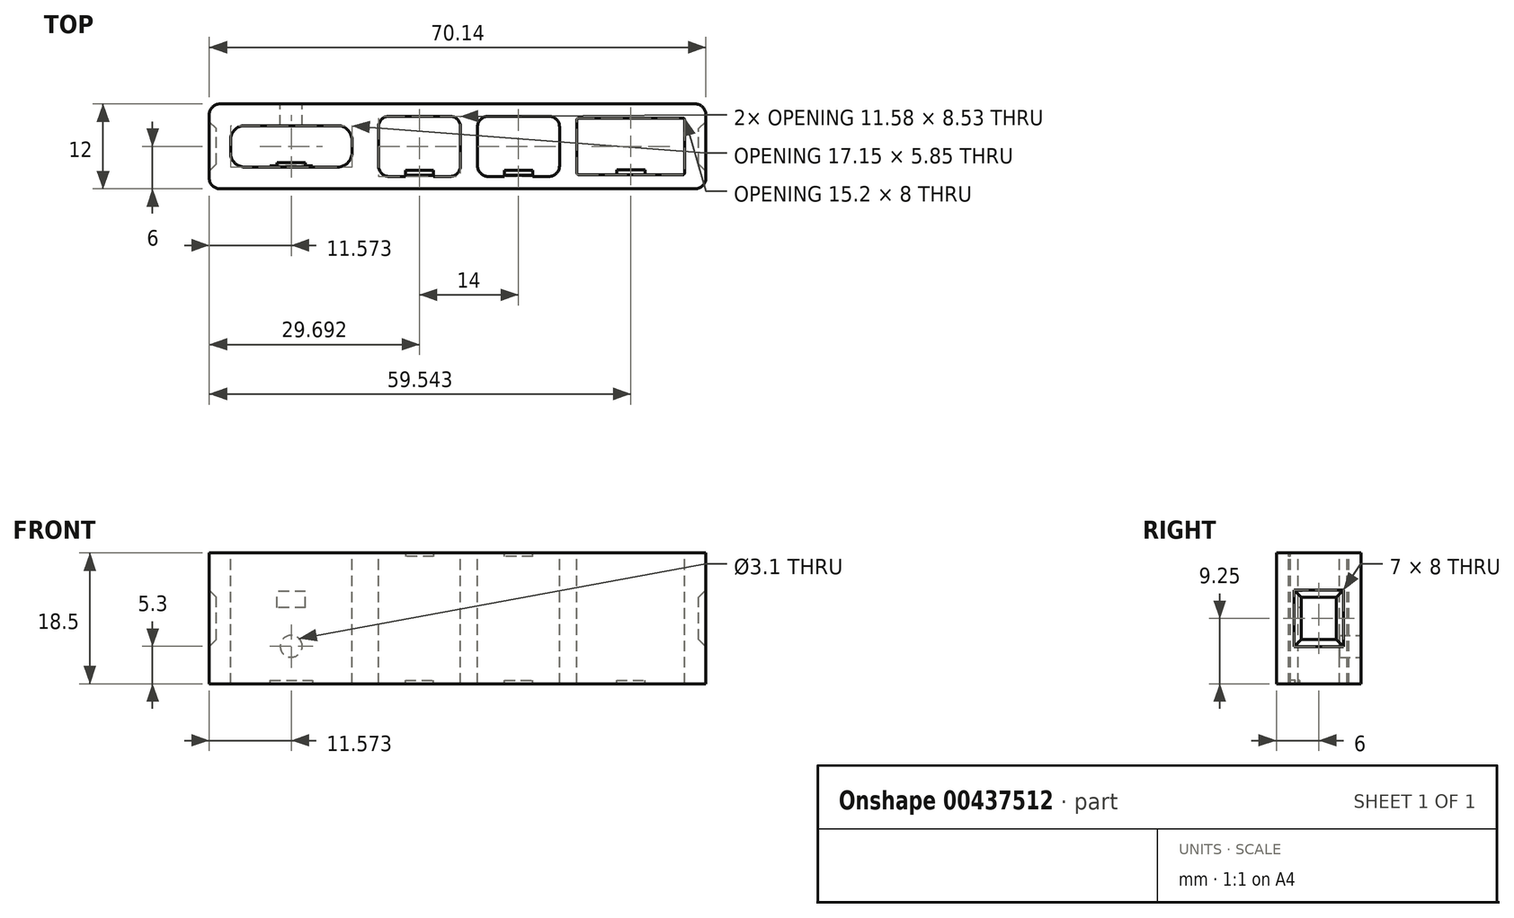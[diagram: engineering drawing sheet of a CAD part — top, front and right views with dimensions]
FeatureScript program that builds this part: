
annotation { "Feature Type Name" : "Feature", "Feature Type Description" : "" }
export const myFeature = defineFeature(function(context is Context, id is Id, definition is map)
    precondition{}
    {
        {
            assignVariable(context, id + "F0", {"name" : "TB1CableStopHeight", "anyValue" : .2});
        }
        {
            var Q0;
            Q0=qCreatedBy(makeId("Front.planeOp"),FACE);
            var sketch = newSketch(context, id + "F1", { "sketchPlane" : qUnion([Q0])});
            skLineSegment(sketch, "E0.bottom", {"start": v(33.57, -6) * mm, "end": v(-33.57, -6) * mm});
            skLineSegment(sketch, "E0.top", {"start": v(33.57, 6) * mm, "end": v(-33.57, 6) * mm});
            skLineSegment(sketch, "E0.left", {"start": v(35.07, -4.5) * mm, "end": v(35.07, 4.5) * mm});
            skLineSegment(sketch, "E0.right", {"start": v(-35.07, -4.5) * mm, "end": v(-35.07, 4.5) * mm});
            skPoint(sketch, "E0.middle", {"position": v(0, 0) * mm});
            skLineSegment(sketch, "E1", {"start": v(-35.07, 0) * mm, "end": v(35.07, 0) * mm, "construction": true});
            skLineSegment(sketch, "E2.bottom", {"start": v(-16.92, -2.92) * mm, "end": v(-30.07, -2.92) * mm});
            skLineSegment(sketch, "E2.top", {"start": v(-16.92, 2.93) * mm, "end": v(-30.07, 2.93) * mm});
            skLineSegment(sketch, "E2.left", {"start": v(-14.92, -0.92) * mm, "end": v(-14.92, 0.93) * mm});
            skLineSegment(sketch, "E2.right", {"start": v(-32.07, -0.92) * mm, "end": v(-32.07, 0.93) * mm});
            skPoint(sketch, "E2.middle", {"position": v(-23.5, 0) * mm});
            skLineSegment(sketch, "E3.bottom", {"start": v(-1.09, 4.26) * mm, "end": v(-9.67, 4.27) * mm});
            skLineSegment(sketch, "E3.top", {"start": v(-1.09, -4.26) * mm, "end": v(-9.67, -4.26) * mm});
            skLineSegment(sketch, "E3.left", {"start": v(0.41, 2.76) * mm, "end": v(0.41, -2.77) * mm});
            skLineSegment(sketch, "E3.right", {"start": v(-11.17, 2.76) * mm, "end": v(-11.17, -2.76) * mm});
            skPoint(sketch, "E3.middle", {"position": v(-5.38, 0) * mm});
            skLineSegment(sketch, "E4.bottom", {"start": v(12.91, 4.27) * mm, "end": v(4.33, 4.27) * mm});
            skLineSegment(sketch, "E4.top", {"start": v(12.91, -4.26) * mm, "end": v(4.33, -4.26) * mm});
            skLineSegment(sketch, "E4.left", {"start": v(14.41, 2.77) * mm, "end": v(14.41, -2.76) * mm});
            skLineSegment(sketch, "E4.right", {"start": v(2.83, 2.77) * mm, "end": v(2.83, -2.76) * mm});
            skPoint(sketch, "E4.middle", {"position": v(8.62, 0) * mm});
            skLineSegment(sketch, "E5.bottom", {"start": v(31.87, -4) * mm, "end": v(17.07, -4) * mm});
            skLineSegment(sketch, "E5.top", {"start": v(31.87, 4) * mm, "end": v(17.07, 4) * mm});
            skLineSegment(sketch, "E5.left", {"start": v(32.07, -3.8) * mm, "end": v(32.07, 3.8) * mm});
            skLineSegment(sketch, "E5.right", {"start": v(16.87, -3.8) * mm, "end": v(16.87, 3.8) * mm});
            skPoint(sketch, "E5.middle", {"position": v(24.47, 0) * mm});
            skPoint(sketch, "E6.visualSharp", {"position": v(-32.07, 2.93) * mm});
            skArc(sketch, "E6.filletArc", {"start": v(-30.07, 2.93) * mm, "mid": v(-31.49, 2.34) * mm, "end": v(-32.07, 0.93) * mm});
            skPoint(sketch, "E7.visualSharp", {"position": v(-14.92, 2.93) * mm});
            skArc(sketch, "E7.filletArc", {"start": v(-14.92, 0.93) * mm, "mid": v(-15.5, 2.34) * mm, "end": v(-16.92, 2.93) * mm});
            skPoint(sketch, "E8.visualSharp", {"position": v(-14.92, -2.92) * mm});
            skArc(sketch, "E8.filletArc", {"start": v(-16.92, -2.92) * mm, "mid": v(-15.5, -2.34) * mm, "end": v(-14.92, -0.92) * mm});
            skPoint(sketch, "E9.visualSharp", {"position": v(-32.07, -2.93) * mm});
            skArc(sketch, "E9.filletArc", {"start": v(-32.07, -0.92) * mm, "mid": v(-31.49, -2.34) * mm, "end": v(-30.07, -2.92) * mm});
            skPoint(sketch, "E10.visualSharp", {"position": v(-11.17, 4.27) * mm});
            skArc(sketch, "E10.filletArc", {"start": v(-9.67, 4.26) * mm, "mid": v(-10.73, 3.83) * mm, "end": v(-11.17, 2.77) * mm});
            skPoint(sketch, "E11.visualSharp", {"position": v(0.41, 4.26) * mm});
            skArc(sketch, "E11.filletArc", {"start": v(0.41, 2.76) * mm, "mid": v(-0.03, 3.83) * mm, "end": v(-1.09, 4.26) * mm});
            skPoint(sketch, "E12.visualSharp", {"position": v(-11.17, -4.26) * mm});
            skArc(sketch, "E12.filletArc", {"start": v(-11.17, -2.76) * mm, "mid": v(-10.73, -3.83) * mm, "end": v(-9.67, -4.26) * mm});
            skPoint(sketch, "E13.visualSharp", {"position": v(0.41, -4.27) * mm});
            skArc(sketch, "E13.filletArc", {"start": v(-1.09, -4.26) * mm, "mid": v(-0.03, -3.83) * mm, "end": v(0.41, -2.77) * mm});
            skPoint(sketch, "E14.visualSharp", {"position": v(2.83, 4.26) * mm});
            skArc(sketch, "E14.filletArc", {"start": v(4.33, 4.26) * mm, "mid": v(3.27, 3.83) * mm, "end": v(2.83, 2.77) * mm});
            skPoint(sketch, "E15.visualSharp", {"position": v(14.41, 4.27) * mm});
            skArc(sketch, "E15.filletArc", {"start": v(14.41, 2.77) * mm, "mid": v(13.97, 3.83) * mm, "end": v(12.91, 4.27) * mm});
            skPoint(sketch, "E16.visualSharp", {"position": v(14.41, -4.26) * mm});
            skArc(sketch, "E16.filletArc", {"start": v(12.91, -4.26) * mm, "mid": v(13.97, -3.83) * mm, "end": v(14.41, -2.76) * mm});
            skPoint(sketch, "E17.visualSharp", {"position": v(2.83, -4.26) * mm});
            skArc(sketch, "E17.filletArc", {"start": v(2.83, -2.76) * mm, "mid": v(3.27, -3.83) * mm, "end": v(4.33, -4.26) * mm});
            skPoint(sketch, "E18.visualSharp", {"position": v(16.87, 4) * mm});
            skArc(sketch, "E18.filletArc", {"start": v(17.07, 4) * mm, "mid": v(16.93, 3.94) * mm, "end": v(16.87, 3.8) * mm});
            skPoint(sketch, "E19.visualSharp", {"position": v(32.07, 4) * mm});
            skArc(sketch, "E19.filletArc", {"start": v(32.07, 3.8) * mm, "mid": v(32.01, 3.94) * mm, "end": v(31.87, 4) * mm});
            skPoint(sketch, "E20.visualSharp", {"position": v(32.07, -4) * mm});
            skArc(sketch, "E20.filletArc", {"start": v(31.87, -4) * mm, "mid": v(32.01, -3.94) * mm, "end": v(32.07, -3.8) * mm});
            skPoint(sketch, "E21.visualSharp", {"position": v(16.87, -4) * mm});
            skArc(sketch, "E21.filletArc", {"start": v(16.87, -3.8) * mm, "mid": v(16.93, -3.94) * mm, "end": v(17.07, -4) * mm});
            skPoint(sketch, "E22.visualSharp", {"position": v(-35.07, 6) * mm});
            skArc(sketch, "E22.filletArc", {"start": v(-33.57, 6) * mm, "mid": v(-34.63, 5.56) * mm, "end": v(-35.07, 4.5) * mm});
            skPoint(sketch, "E23.visualSharp", {"position": v(35.07, 6) * mm});
            skArc(sketch, "E23.filletArc", {"start": v(35.07, 4.5) * mm, "mid": v(34.63, 5.56) * mm, "end": v(33.57, 6) * mm});
            skPoint(sketch, "E24.visualSharp", {"position": v(35.07, -6) * mm});
            skArc(sketch, "E24.filletArc", {"start": v(33.57, -6) * mm, "mid": v(34.63, -5.56) * mm, "end": v(35.07, -4.5) * mm});
            skPoint(sketch, "E25.visualSharp", {"position": v(-35.07, -6) * mm});
            skArc(sketch, "E25.filletArc", {"start": v(-35.07, -4.5) * mm, "mid": v(-34.63, -5.56) * mm, "end": v(-33.57, -6) * mm});
            skSolve(sketch);
        }
        {
            var Q0;
            Q0=makeQuery(id+"F1.imprint","IMPRINT",FACE,{"disambiguationData":[TD([[makeQuery(id+"F1.imprint","IMPRINT",EDGE,{"derivedFrom":sQuery(id+"F1.wireOp",EDGE,"E0.bottom")}),-1.0]])]});
            extrude(context, id + "F2", {"entities" : qUnion([Q0]), "oppositeDirection" : true, "depth" : 18.5 * mm});
        }
        {
            var Q0;
            Q0=makeQuery(id+"F2.opExtrude","SWEPT_FACE",FACE,{"disambiguationData":[OSD([sQuery(id+"F1.wireOp",EDGE,"E0.top")])]});
            var sketch = newSketch(context, id + "F3", { "sketchPlane" : qUnion([Q0])});
            skPoint(sketch, "E26.0", {"position": v(-23.5, 0) * mm});
            skCircle(sketch, "E27", {"center": v(-23.5, 13.2) * mm, "radius": 1.55 * mm});
            skPoint(sketch, "E28.0", {"position": v(33.57, 9.25) * mm});
            skLineSegment(sketch, "E29.bottom", {"start": v(3.5, 13.25) * mm, "end": v(-3.5, 13.25) * mm});
            skLineSegment(sketch, "E29.top", {"start": v(3.5, 5.25) * mm, "end": v(-3.5, 5.25) * mm});
            skLineSegment(sketch, "E29.left", {"start": v(3.5, 13.25) * mm, "end": v(3.5, 5.25) * mm});
            skLineSegment(sketch, "E29.right", {"start": v(-3.5, 13.25) * mm, "end": v(-3.5, 5.25) * mm});
            skPoint(sketch, "E29.middle", {"position": v(0, 9.25) * mm});
            skSolve(sketch);
        }
        {
            var Q0;
            Q0=makeQuery(id+"F3.imprint","IMPRINT",FACE,{"disambiguationData":[TD([[makeQuery(id+"F3.imprint","IMPRINT",EDGE,{"derivedFrom":sQuery(id+"F3.wireOp",EDGE,"E27")}),1.0]])]});
            extrude(context, id + "F4", {"entities" : qUnion([Q0]), "operationType" : NewBodyOperationType.REMOVE, "endBound" : BoundingType.UP_TO_NEXT, "oppositeDirection" : true, "depth" : 25 * mm});
        }
        {
            var Q0;
            Q0=makeQuery(id+"F2.opExtrude","SWEPT_FACE",FACE,{"disambiguationData":[OSD([sQuery(id+"F1.wireOp",EDGE,"E2.bottom")])]});
            var sketch = newSketch(context, id + "F5", { "sketchPlane" : qUnion([Q0])});
            skPoint(sketch, "E30.0", {"position": v(-23.5, 0) * mm});
            skLineSegment(sketch, "E31.bottom", {"start": v(-26.5, 18) * mm, "end": v(-20.5, 18) * mm});
            skLineSegment(sketch, "E31.top", {"start": v(-26.5, 18.5) * mm, "end": v(-20.5, 18.5) * mm});
            skLineSegment(sketch, "E31.left", {"start": v(-26.5, 18) * mm, "end": v(-26.5, 18.5) * mm});
            skLineSegment(sketch, "E31.right", {"start": v(-20.5, 18) * mm, "end": v(-20.5, 18.5) * mm});
            skPoint(sketch, "E31.middle", {"position": v(-23.5, 18.25) * mm});
            skLineSegment(sketch, "E32.0", {"start": v(-16.92, 18.5) * mm, "end": v(-30.07, 18.5) * mm});
            skLineSegment(sketch, "E33.bottom", {"start": v(-21.5, 7.7) * mm, "end": v(-25.5, 7.7) * mm});
            skLineSegment(sketch, "E33.top", {"start": v(-21.5, 5.45) * mm, "end": v(-25.5, 5.45) * mm});
            skLineSegment(sketch, "E33.left", {"start": v(-21.5, 7.7) * mm, "end": v(-21.5, 5.45) * mm});
            skLineSegment(sketch, "E33.right", {"start": v(-25.5, 7.7) * mm, "end": v(-25.5, 5.45) * mm});
            skPoint(sketch, "E33.middle", {"position": v(-23.5, 6.57) * mm});
            skSolve(sketch);
        }
        {
            var Q0;
            Q0=makeQuery(id+"F5.imprint","IMPRINT",FACE,{"disambiguationData":[TD([[makeQuery(id+"F5.imprint","IMPRINT",EDGE,{"derivedFrom":sQuery(id+"F5.wireOp",EDGE,"E31.bottom")}),1.0]])]});
            extrude(context, id + "F6", {"entities" : qUnion([Q0]), "operationType" : NewBodyOperationType.ADD, "depth" : .2 * mm});
        }
        {
            var Q0;
            Q0=makeQuery(id+"F5.imprint","IMPRINT",FACE,{"disambiguationData":[TD([[makeQuery(id+"F5.imprint","IMPRINT",EDGE,{"derivedFrom":sQuery(id+"F5.wireOp",EDGE,"E33.bottom")}),1.0]])]});
            extrude(context, id + "F7", {"entities" : qUnion([Q0]), "operationType" : NewBodyOperationType.ADD, "depth" : .6 * mm});
        }
        {
            var Q0;
            Q0=makeQuery(id+"F2.opExtrude","SWEPT_FACE",FACE,{"disambiguationData":[OSD([sQuery(id+"F1.wireOp",EDGE,"E3.top")])]});
            var sketch = newSketch(context, id + "F8", { "sketchPlane" : qUnion([Q0])});
            skPoint(sketch, "E34.0", {"position": v(-5.38, 0) * mm});
            skLineSegment(sketch, "E35.bottom", {"start": v(-7.38, 18.5) * mm, "end": v(-3.38, 18.5) * mm});
            skLineSegment(sketch, "E35.top", {"start": v(-7.38, 18) * mm, "end": v(-3.38, 18) * mm});
            skLineSegment(sketch, "E35.left", {"start": v(-7.38, 18.5) * mm, "end": v(-7.38, 18) * mm});
            skLineSegment(sketch, "E35.right", {"start": v(-3.38, 18.5) * mm, "end": v(-3.38, 18) * mm});
            skPoint(sketch, "E35.middle", {"position": v(-5.38, 18.25) * mm});
            skLineSegment(sketch, "E36.bottom", {"start": v(-3.38, -1.03) * mm, "end": v(-7.38, -1.03) * mm});
            skLineSegment(sketch, "E36.top", {"start": v(-3.38, 0.47) * mm, "end": v(-7.38, 0.47) * mm});
            skLineSegment(sketch, "E36.left", {"start": v(-3.38, -1.03) * mm, "end": v(-3.38, 0.47) * mm});
            skLineSegment(sketch, "E36.right", {"start": v(-7.38, -1.03) * mm, "end": v(-7.38, 0.47) * mm});
            skPoint(sketch, "E36.middle", {"position": v(-5.38, -0.28) * mm});
            skLineSegment(sketch, "E37.0", {"start": v(-1.09, 18.5) * mm, "end": v(-9.67, 18.5) * mm});
            skSolve(sketch);
        }
        {
            var Q0;
            Q0=makeQuery(id+"F8.imprint","IMPRINT",FACE,{"disambiguationData":[TD([[makeQuery(id+"F8.imprint","IMPRINT",EDGE,{"derivedFrom":sQuery(id+"F8.wireOp",EDGE,"E35.top")}),1.0]])]});
            extrude(context, id + "F9", {"entities" : qUnion([Q0]), "operationType" : NewBodyOperationType.ADD, "depth" : .9 * mm});
        }
        {
            var Q0;
            {var subQ0=sQuery(id+"F8.wireOp",EDGE,"E36.top");Q0=makeQuery(id+"F8.imprint","IMPRINT",FACE,{"disambiguationData":[TD([[makeQuery(id+"F8.imprint","IMPRINT",EDGE,{"derivedFrom":subQ0}),1.0]])]});}
            extrude(context, id + "F10", {"entities" : qUnion([Q0]), "operationType" : NewBodyOperationType.ADD, "depth" : (getVariable(context, 'TB1CableStopHeight')) * mm});
        }
        {
            var Q0;
            Q0=makeQuery(id+"F2.opExtrude","SWEPT_FACE",FACE,{"disambiguationData":[OSD([sQuery(id+"F1.wireOp",EDGE,"E4.top")])]});
            var sketch = newSketch(context, id + "F11", { "sketchPlane" : qUnion([Q0])});
            skPoint(sketch, "E38.0", {"position": v(8.62, 0) * mm});
            skLineSegment(sketch, "E39.bottom", {"start": v(6.62, 18.5) * mm, "end": v(10.62, 18.5) * mm});
            skLineSegment(sketch, "E39.top", {"start": v(6.62, 18) * mm, "end": v(10.62, 18) * mm});
            skLineSegment(sketch, "E39.left", {"start": v(6.62, 18.5) * mm, "end": v(6.62, 18) * mm});
            skLineSegment(sketch, "E39.right", {"start": v(10.62, 18.5) * mm, "end": v(10.62, 18) * mm});
            skPoint(sketch, "E39.middle", {"position": v(8.62, 18.25) * mm});
            skLineSegment(sketch, "E40.bottom", {"start": v(10.62, 0.47) * mm, "end": v(6.62, 0.47) * mm});
            skLineSegment(sketch, "E40.top", {"start": v(10.62, -1.03) * mm, "end": v(6.62, -1.03) * mm});
            skLineSegment(sketch, "E40.left", {"start": v(10.62, 0.47) * mm, "end": v(10.62, -1.03) * mm});
            skLineSegment(sketch, "E40.right", {"start": v(6.62, 0.47) * mm, "end": v(6.62, -1.03) * mm});
            skPoint(sketch, "E40.middle", {"position": v(8.62, -0.28) * mm});
            skLineSegment(sketch, "E41.0", {"start": v(12.91, 18.5) * mm, "end": v(4.33, 18.5) * mm});
            skSolve(sketch);
        }
        {
            var Q0;
            Q0=makeQuery(id+"F11.imprint","IMPRINT",FACE,{"disambiguationData":[TD([[makeQuery(id+"F11.imprint","IMPRINT",EDGE,{"derivedFrom":sQuery(id+"F11.wireOp",EDGE,"E39.top")}),1.0]])]});
            extrude(context, id + "F12", {"entities" : qUnion([Q0]), "operationType" : NewBodyOperationType.ADD, "depth" : .9 * mm});
        }
        {
            var Q0;
            Q0=makeQuery(id+"F11.imprint","IMPRINT",FACE,{"disambiguationData":[TD([[makeQuery(id+"F11.imprint","IMPRINT",EDGE,{"derivedFrom":sQuery(id+"F11.wireOp",EDGE,"E40.bottom")}),1.0]])]});
            extrude(context, id + "F13", {"entities" : qUnion([Q0]), "operationType" : NewBodyOperationType.ADD, "depth" : (getVariable(context, 'TB1CableStopHeight')) * mm});
        }
        {
            var Q0;
            Q0=makeQuery(id+"F2.opExtrude","SWEPT_FACE",FACE,{"disambiguationData":[OSD([sQuery(id+"F1.wireOp",EDGE,"E5.bottom")])]});
            var sketch = newSketch(context, id + "F14", { "sketchPlane" : qUnion([Q0])});
            skPoint(sketch, "E42.0", {"position": v(24.47, 0) * mm});
            skLineSegment(sketch, "E43.bottom", {"start": v(22.47, 18.5) * mm, "end": v(26.47, 18.5) * mm});
            skLineSegment(sketch, "E43.top", {"start": v(22.47, 18) * mm, "end": v(26.47, 18) * mm});
            skLineSegment(sketch, "E43.left", {"start": v(22.47, 18.5) * mm, "end": v(22.47, 18) * mm});
            skLineSegment(sketch, "E43.right", {"start": v(26.47, 18.5) * mm, "end": v(26.47, 18) * mm});
            skPoint(sketch, "E43.middle", {"position": v(24.47, 18.25) * mm});
            skSolve(sketch);
        }
        {
            var Q0;
            Q0=makeQuery(id+"F14.imprint","IMPRINT",FACE,{"disambiguationData":[TD([[makeQuery(id+"F14.imprint","IMPRINT",EDGE,{"derivedFrom":sQuery(id+"F14.wireOp",EDGE,"E43.bottom")}),1.0]])]});
            extrude(context, id + "F15", {"entities" : qUnion([Q0]), "operationType" : NewBodyOperationType.ADD, "depth" : .7 * mm});
        }
        {
            var Q0;
            Q0=makeQuery(id+"F2.opExtrude","SWEPT_FACE",FACE,{"disambiguationData":[OSD([sQuery(id+"F1.wireOp",EDGE,"E0.left")])]});
            var sketch = newSketch(context, id + "F16", { "sketchPlane" : qUnion([Q0])});
            skPoint(sketch, "E44.0", {"position": v(9.25, 6) * mm});
            skPoint(sketch, "E45.0", {"position": v(18.5, 0) * mm});
            skLineSegment(sketch, "E46.bottom", {"start": v(13.25, 3.5) * mm, "end": v(5.25, 3.5) * mm});
            skLineSegment(sketch, "E46.top", {"start": v(13.25, -3.5) * mm, "end": v(5.25, -3.5) * mm});
            skLineSegment(sketch, "E46.left", {"start": v(13.25, 3.5) * mm, "end": v(13.25, -3.5) * mm});
            skLineSegment(sketch, "E46.right", {"start": v(5.25, 3.5) * mm, "end": v(5.25, -3.5) * mm});
            skPoint(sketch, "E46.middle", {"position": v(9.25, 0) * mm});
            skSolve(sketch);
        }
        {
            var Q0;
            Q0=qSketchRegion(id+"F16",true);
            extrude(context, id + "F17", {"entities" : qUnion([Q0]), "operationType" : NewBodyOperationType.REMOVE, "oppositeDirection" : true, "depth" : 1 * mm, "hasDraft" : true, "draftAngle" : 45 * degree, "draftPullDirection" : true});
        }
        {
            var Q0;
            Q0=makeQuery(id+"F2.opExtrude","SWEPT_FACE",FACE,{"disambiguationData":[OSD([sQuery(id+"F1.wireOp",EDGE,"E0.right")])]});
            var sketch = newSketch(context, id + "F18", { "sketchPlane" : qUnion([Q0])});
            skPoint(sketch, "E47.0", {"position": v(-9.25, 6) * mm});
            skPoint(sketch, "E48.0", {"position": v(0, 0) * mm});
            skLineSegment(sketch, "E49.bottom", {"start": v(-5.25, -3.5) * mm, "end": v(-13.25, -3.5) * mm});
            skLineSegment(sketch, "E49.top", {"start": v(-5.25, 3.5) * mm, "end": v(-13.25, 3.5) * mm});
            skLineSegment(sketch, "E49.left", {"start": v(-5.25, -3.5) * mm, "end": v(-5.25, 3.5) * mm});
            skLineSegment(sketch, "E49.right", {"start": v(-13.25, -3.5) * mm, "end": v(-13.25, 3.5) * mm});
            skPoint(sketch, "E49.middle", {"position": v(-9.25, 0) * mm});
            skSolve(sketch);
        }
        {
            var Q0;
            Q0=qSketchRegion(id+"F18",true);
            extrude(context, id + "F19", {"entities" : qUnion([Q0]), "operationType" : NewBodyOperationType.REMOVE, "oppositeDirection" : true, "depth" : 1 * mm, "hasDraft" : true, "draftAngle" : 45 * degree, "draftPullDirection" : true});
        }
        {
            var Q0;
            Q0=makeQuery(id+"F2.opExtrude","SWEPT_FACE",FACE,{"disambiguationData":[OSD([sQuery(id+"F1.wireOp",EDGE,"E0.bottom")])]});
            var sketch = newSketch(context, id + "F20", { "sketchPlane" : qUnion([Q0])});
            skPoint(sketch, "E50.0", {"position": v(-38.78, -17.75) * mm});
            skPoint(sketch, "E51.0", {"position": v(0, 0) * mm});
            skPoint(sketch, "E52.0", {"position": v(33.57, -9.25) * mm});
            skLineSegment(sketch, "E53.bottom", {"start": v(4, -5.75) * mm, "end": v(-4, -5.75) * mm});
            skLineSegment(sketch, "E53.top", {"start": v(4, -12.75) * mm, "end": v(-4, -12.75) * mm});
            skLineSegment(sketch, "E53.left", {"start": v(4, -5.75) * mm, "end": v(4, -12.75) * mm});
            skLineSegment(sketch, "E53.right", {"start": v(-4, -5.75) * mm, "end": v(-4, -12.75) * mm});
            skPoint(sketch, "E53.middle", {"position": v(0, -9.25) * mm});
            skText(sketch, "E54", { "text": "JS", "fontName": "OpenSans-Regular.ttf"});
            const initialGuessF20  = {"E54": [0.0279, -0.01727, 1, 0, 0.00333]};
            skSetInitialGuess(sketch, initialGuessF20);
            skSolve(sketch);
        }
        {
            var Q0;
            Q0=makeQuery(id+"F15.boolean.opBoolean","MERGE",FACE,{"derivedFrom":[makeQuery(id+"F12.boolean.opBoolean","MERGE",FACE,{"derivedFrom":[makeQuery(id+"F9.boolean.opBoolean","MERGE",FACE,{"derivedFrom":[makeQuery(id+"F6.boolean.opBoolean","MERGE",FACE,{"derivedFrom":[makeQuery(id+"F2.opExtrude","CAP_FACE",FACE,{"disambiguationData":[OSD([sQuery(id+"F1.wireOp",EDGE,"E0.bottom"),sQuery(id+"F1.wireOp",EDGE,"E0.top"),sQuery(id+"F1.wireOp",EDGE,"E0.left"),sQuery(id+"F1.wireOp",EDGE,"E0.right"),sQuery(id+"F1.wireOp",EDGE,"E2.bottom"),sQuery(id+"F1.wireOp",EDGE,"E2.top"),sQuery(id+"F1.wireOp",EDGE,"E2.left"),sQuery(id+"F1.wireOp",EDGE,"E2.right"),sQuery(id+"F1.wireOp",EDGE,"E3.bottom"),sQuery(id+"F1.wireOp",EDGE,"E3.top"),sQuery(id+"F1.wireOp",EDGE,"E3.left"),sQuery(id+"F1.wireOp",EDGE,"E3.right"),sQuery(id+"F1.wireOp",EDGE,"E4.bottom"),sQuery(id+"F1.wireOp",EDGE,"E4.top"),sQuery(id+"F1.wireOp",EDGE,"E4.left"),sQuery(id+"F1.wireOp",EDGE,"E4.right"),sQuery(id+"F1.wireOp",EDGE,"E5.bottom"),sQuery(id+"F1.wireOp",EDGE,"E5.top"),sQuery(id+"F1.wireOp",EDGE,"E5.left"),sQuery(id+"F1.wireOp",EDGE,"E5.right"),sQuery(id+"F1.wireOp",EDGE,"E6.filletArc"),sQuery(id+"F1.wireOp",EDGE,"E7.filletArc"),sQuery(id+"F1.wireOp",EDGE,"E8.filletArc"),sQuery(id+"F1.wireOp",EDGE,"E9.filletArc"),sQuery(id+"F1.wireOp",EDGE,"E10.filletArc"),sQuery(id+"F1.wireOp",EDGE,"E11.filletArc"),sQuery(id+"F1.wireOp",EDGE,"E12.filletArc"),sQuery(id+"F1.wireOp",EDGE,"E13.filletArc"),sQuery(id+"F1.wireOp",EDGE,"E14.filletArc"),sQuery(id+"F1.wireOp",EDGE,"E15.filletArc"),sQuery(id+"F1.wireOp",EDGE,"E16.filletArc"),sQuery(id+"F1.wireOp",EDGE,"E17.filletArc"),sQuery(id+"F1.wireOp",EDGE,"E18.filletArc"),sQuery(id+"F1.wireOp",EDGE,"E19.filletArc"),sQuery(id+"F1.wireOp",EDGE,"E20.filletArc"),sQuery(id+"F1.wireOp",EDGE,"E21.filletArc"),sQuery(id+"F1.wireOp",EDGE,"E22.filletArc"),sQuery(id+"F1.wireOp",EDGE,"E23.filletArc"),sQuery(id+"F1.wireOp",EDGE,"E24.filletArc"),sQuery(id+"F1.wireOp",EDGE,"E25.filletArc")])],"isStart":false}),makeQuery(id+"F6.opExtrude","SWEPT_FACE",FACE,{"disambiguationData":[OSD([sQuery(id+"F5.wireOp",EDGE,"E32.0")])]})]}),makeQuery(id+"F9.opExtrude","SWEPT_FACE",FACE,{"disambiguationData":[OSD([sQuery(id+"F8.wireOp",EDGE,"E37.0")])]})]}),makeQuery(id+"F12.opExtrude","SWEPT_FACE",FACE,{"disambiguationData":[OSD([sQuery(id+"F11.wireOp",EDGE,"E41.0")])]})]}),makeQuery(id+"F15.opExtrude","SWEPT_FACE",FACE,{"disambiguationData":[OSD([sQuery(id+"F14.wireOp",EDGE,"E43.bottom")])]})]});
            var sketch = newSketch(context, id + "F21", { "sketchPlane" : qUnion([Q0])});
            skCircle(sketch, "E55", {"center": v(-34.63, 5.56) * mm, "radius": 3 * mm});
            skCircle(sketch, "E56", {"center": v(34.63, 5.56) * mm, "radius": 3 * mm});
            skCircle(sketch, "E57", {"center": v(34.63, -5.56) * mm, "radius": 3 * mm});
            skCircle(sketch, "E58", {"center": v(-34.63, -5.56) * mm, "radius": 3 * mm});
            skSolve(sketch);
        }
        {
            var Q0;
            Q0=makeQuery(id+"F2.opExtrude","SWEPT_BODY",BODY,{"disambiguationData":[OSD([sQuery(id+"F1.wireOp",EDGE,"E0.bottom"),sQuery(id+"F1.wireOp",EDGE,"E0.top"),sQuery(id+"F1.wireOp",EDGE,"E0.left"),sQuery(id+"F1.wireOp",EDGE,"E0.right"),sQuery(id+"F1.wireOp",EDGE,"E2.bottom"),sQuery(id+"F1.wireOp",EDGE,"E2.top"),sQuery(id+"F1.wireOp",EDGE,"E2.left"),sQuery(id+"F1.wireOp",EDGE,"E2.right"),sQuery(id+"F1.wireOp",EDGE,"E3.bottom"),sQuery(id+"F1.wireOp",EDGE,"E3.top"),sQuery(id+"F1.wireOp",EDGE,"E3.left"),sQuery(id+"F1.wireOp",EDGE,"E3.right"),sQuery(id+"F1.wireOp",EDGE,"E4.bottom"),sQuery(id+"F1.wireOp",EDGE,"E4.top"),sQuery(id+"F1.wireOp",EDGE,"E4.left"),sQuery(id+"F1.wireOp",EDGE,"E4.right"),sQuery(id+"F1.wireOp",EDGE,"E5.bottom"),sQuery(id+"F1.wireOp",EDGE,"E5.top"),sQuery(id+"F1.wireOp",EDGE,"E5.left"),sQuery(id+"F1.wireOp",EDGE,"E5.right"),sQuery(id+"F1.wireOp",EDGE,"E6.filletArc"),sQuery(id+"F1.wireOp",EDGE,"E7.filletArc"),sQuery(id+"F1.wireOp",EDGE,"E8.filletArc"),sQuery(id+"F1.wireOp",EDGE,"E9.filletArc"),sQuery(id+"F1.wireOp",EDGE,"E10.filletArc"),sQuery(id+"F1.wireOp",EDGE,"E11.filletArc"),sQuery(id+"F1.wireOp",EDGE,"E12.filletArc"),sQuery(id+"F1.wireOp",EDGE,"E13.filletArc"),sQuery(id+"F1.wireOp",EDGE,"E14.filletArc"),sQuery(id+"F1.wireOp",EDGE,"E15.filletArc"),sQuery(id+"F1.wireOp",EDGE,"E16.filletArc"),sQuery(id+"F1.wireOp",EDGE,"E17.filletArc"),sQuery(id+"F1.wireOp",EDGE,"E18.filletArc"),sQuery(id+"F1.wireOp",EDGE,"E19.filletArc"),sQuery(id+"F1.wireOp",EDGE,"E20.filletArc"),sQuery(id+"F1.wireOp",EDGE,"E21.filletArc"),sQuery(id+"F1.wireOp",EDGE,"E22.filletArc"),sQuery(id+"F1.wireOp",EDGE,"E23.filletArc"),sQuery(id+"F1.wireOp",EDGE,"E24.filletArc"),sQuery(id+"F1.wireOp",EDGE,"E25.filletArc")])]});
            var Q1;
            Q1=makeQuery(id+"F2.opExtrude","CAP_EDGE",EDGE,{"disambiguationData":[OSD([sQuery(id+"F1.wireOp",EDGE,"E0.top")])],"isStart":false});
            transform(context, id + "F22", {"entities" : qUnion([Q0]), "transformType" : TransformType.ROTATION, "transformAxis" : qUnion([Q1]), "angle" : 90 * degree, "makeCopy" : false});
        }
    });
